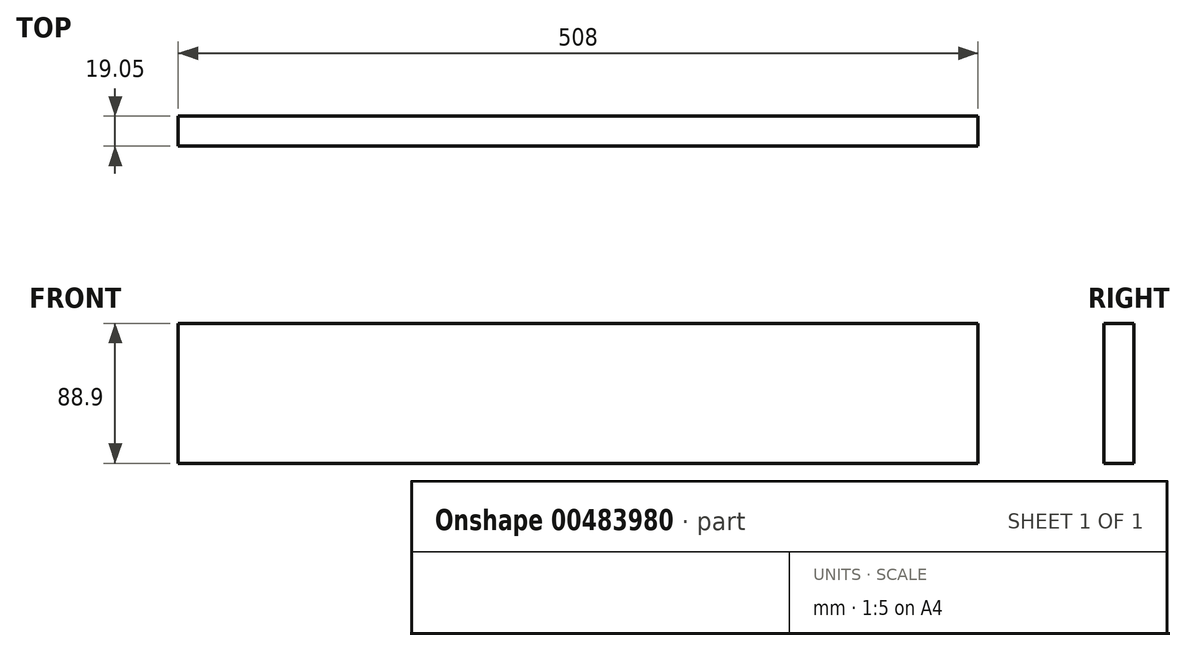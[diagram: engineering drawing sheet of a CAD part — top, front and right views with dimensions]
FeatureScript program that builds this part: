
annotation { "Feature Type Name" : "Feature", "Feature Type Description" : "" }
export const myFeature = defineFeature(function(context is Context, id is Id, definition is map)
    precondition{}
    {
        {
            var Q0;
            Q0=qCreatedBy(makeId("Front.planeOp"),FACE);
            var sketch = newSketch(context, id + "F0", { "sketchPlane" : qUnion([Q0])});
            skLineSegment(sketch, "E0.bottom", {"start": v(254, -44.45) * mm, "end": v(-254, -44.45) * mm});
            skLineSegment(sketch, "E0.top", {"start": v(254, 44.45) * mm, "end": v(-254, 44.45) * mm});
            skLineSegment(sketch, "E0.left", {"start": v(254, -44.45) * mm, "end": v(254, 44.45) * mm});
            skLineSegment(sketch, "E0.right", {"start": v(-254, -44.45) * mm, "end": v(-254, 44.45) * mm});
            skPoint(sketch, "E0.middle", {"position": v(0, 0) * mm});
            skSolve(sketch);
        }
        {
            var Q0;
            Q0 = qSketchRegion(id + "F0", true);
            extrude(context, id + "F1", {"entities" : qUnion([Q0]), "depth" : 19.05 * mm});
        }
    });
